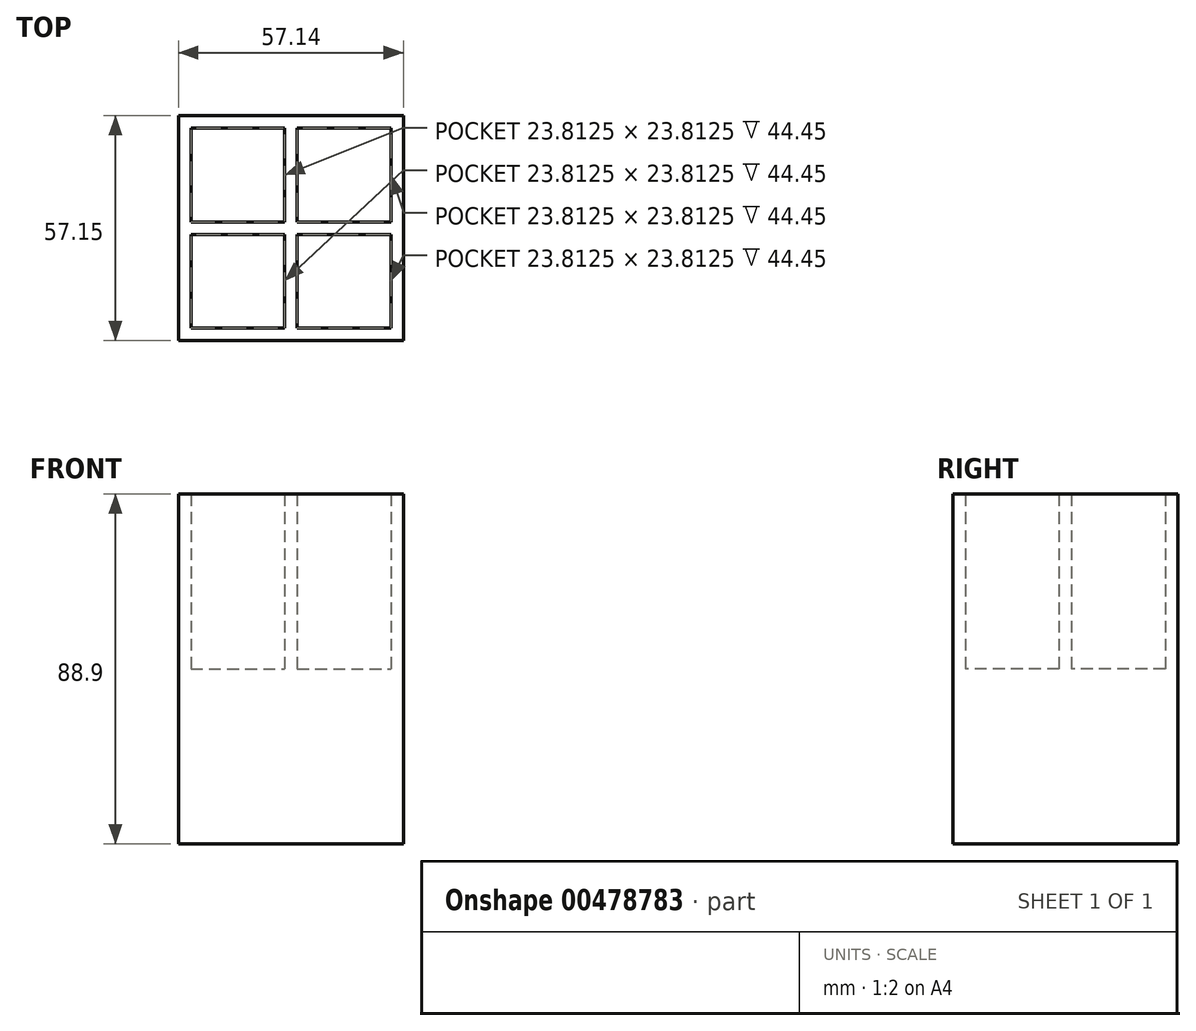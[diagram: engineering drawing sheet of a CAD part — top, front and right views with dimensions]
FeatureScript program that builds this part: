
annotation { "Feature Type Name" : "Feature", "Feature Type Description" : "" }
export const myFeature = defineFeature(function(context is Context, id is Id, definition is map)
    precondition{}
    {
        {
            var Q0;
            Q0=qCreatedBy(makeId("Front.planeOp"),FACE);
            var sketch = newSketch(context, id + "F0", { "sketchPlane" : qUnion([Q0])});
            skLineSegment(sketch, "E0.bottom", {"start": v(28.58, 44.45) * mm, "end": v(-28.58, 44.45) * mm});
            skLineSegment(sketch, "E0.top", {"start": v(28.58, -44.45) * mm, "end": v(-28.58, -44.45) * mm});
            skLineSegment(sketch, "E0.left", {"start": v(28.58, 44.45) * mm, "end": v(28.58, -44.45) * mm});
            skLineSegment(sketch, "E0.right", {"start": v(-28.58, 44.45) * mm, "end": v(-28.58, -44.45) * mm});
            skPoint(sketch, "E0.middle", {"position": v(0, 0) * mm});
            skSolve(sketch);
        }
        {
            var Q0;
            Q0 = qSketchRegion(id + "F0", true);
            extrude(context, id + "F1", {"entities" : qUnion([Q0]), "depth" : 57.15 * mm});
        }
        {
            var Q0;
            Q0=qCreatedBy(makeId("Top.planeOp"),FACE);
            var sketch = newSketch(context, id + "F2", { "sketchPlane" : qUnion([Q0])});
            skLineSegment(sketch, "E1.bottom", {"start": v(-25.4, -3.18) * mm, "end": v(-1.59, -3.17) * mm});
            skLineSegment(sketch, "E1.top", {"start": v(-25.4, -26.99) * mm, "end": v(-1.59, -26.99) * mm});
            skLineSegment(sketch, "E1.left", {"start": v(-25.4, -3.18) * mm, "end": v(-25.4, -26.99) * mm});
            skLineSegment(sketch, "E1.right", {"start": v(-1.59, -3.17) * mm, "end": v(-1.59, -26.99) * mm});
            skSolve(sketch);
        }
        {
            var Q0;
            Q0=qCreatedBy(makeId("Top.planeOp"),FACE);
            var sketch = newSketch(context, id + "F3", { "sketchPlane" : qUnion([Q0])});
            skLineSegment(sketch, "E2.bottom", {"start": v(-1.59, -30.16) * mm, "end": v(-25.4, -30.16) * mm});
            skLineSegment(sketch, "E2.top", {"start": v(-1.59, -53.98) * mm, "end": v(-25.4, -53.98) * mm});
            skLineSegment(sketch, "E2.left", {"start": v(-1.59, -30.16) * mm, "end": v(-1.59, -53.98) * mm});
            skLineSegment(sketch, "E2.right", {"start": v(-25.4, -30.16) * mm, "end": v(-25.4, -53.98) * mm});
            skSolve(sketch);
        }
        {
            var Q0;
            Q0=qCreatedBy(makeId("Top.planeOp"),FACE);
            var sketch = newSketch(context, id + "F4", { "sketchPlane" : qUnion([Q0])});
            skLineSegment(sketch, "E3.bottom", {"start": v(1.59, -3.18) * mm, "end": v(25.4, -3.18) * mm});
            skLineSegment(sketch, "E3.top", {"start": v(1.59, -26.99) * mm, "end": v(25.4, -26.99) * mm});
            skLineSegment(sketch, "E3.left", {"start": v(1.59, -3.18) * mm, "end": v(1.59, -26.99) * mm});
            skLineSegment(sketch, "E3.right", {"start": v(25.4, -3.18) * mm, "end": v(25.4, -26.99) * mm});
            skSolve(sketch);
        }
        {
            var Q0;
            Q0=qCreatedBy(makeId("Top.planeOp"),FACE);
            var sketch = newSketch(context, id + "F5", { "sketchPlane" : qUnion([Q0])});
            skLineSegment(sketch, "E4.bottom", {"start": v(1.59, -30.16) * mm, "end": v(25.4, -30.16) * mm});
            skLineSegment(sketch, "E4.top", {"start": v(1.59, -53.98) * mm, "end": v(25.4, -53.98) * mm});
            skLineSegment(sketch, "E4.left", {"start": v(1.59, -30.16) * mm, "end": v(1.59, -53.98) * mm});
            skLineSegment(sketch, "E4.right", {"start": v(25.4, -30.16) * mm, "end": v(25.4, -53.98) * mm});
            skSolve(sketch);
        }
        {
            var Q0;
            Q0 = qSketchRegion(id + "F2", true);
            extrude(context, id + "F6", {"entities" : qUnion([Q0]), "operationType" : NewBodyOperationType.REMOVE, "endBound" : BoundingType.THROUGH_ALL, "depth" : 25.4 * mm});
        }
        {
            var Q0;
            Q0 = qSketchRegion(id + "F3", true);
            extrude(context, id + "F7", {"entities" : qUnion([Q0]), "operationType" : NewBodyOperationType.REMOVE, "endBound" : BoundingType.THROUGH_ALL, "depth" : 25.4 * mm});
        }
        {
            var Q0;
            Q0 = qSketchRegion(id + "F4", true);
            extrude(context, id + "F8", {"entities" : qUnion([Q0]), "operationType" : NewBodyOperationType.REMOVE, "endBound" : BoundingType.THROUGH_ALL, "depth" : 25.4 * mm});
        }
        {
            var Q0;
            Q0 = qSketchRegion(id + "F5", true);
            extrude(context, id + "F9", {"entities" : qUnion([Q0]), "operationType" : NewBodyOperationType.REMOVE, "endBound" : BoundingType.THROUGH_ALL, "depth" : 25.4 * mm});
        }
    });
